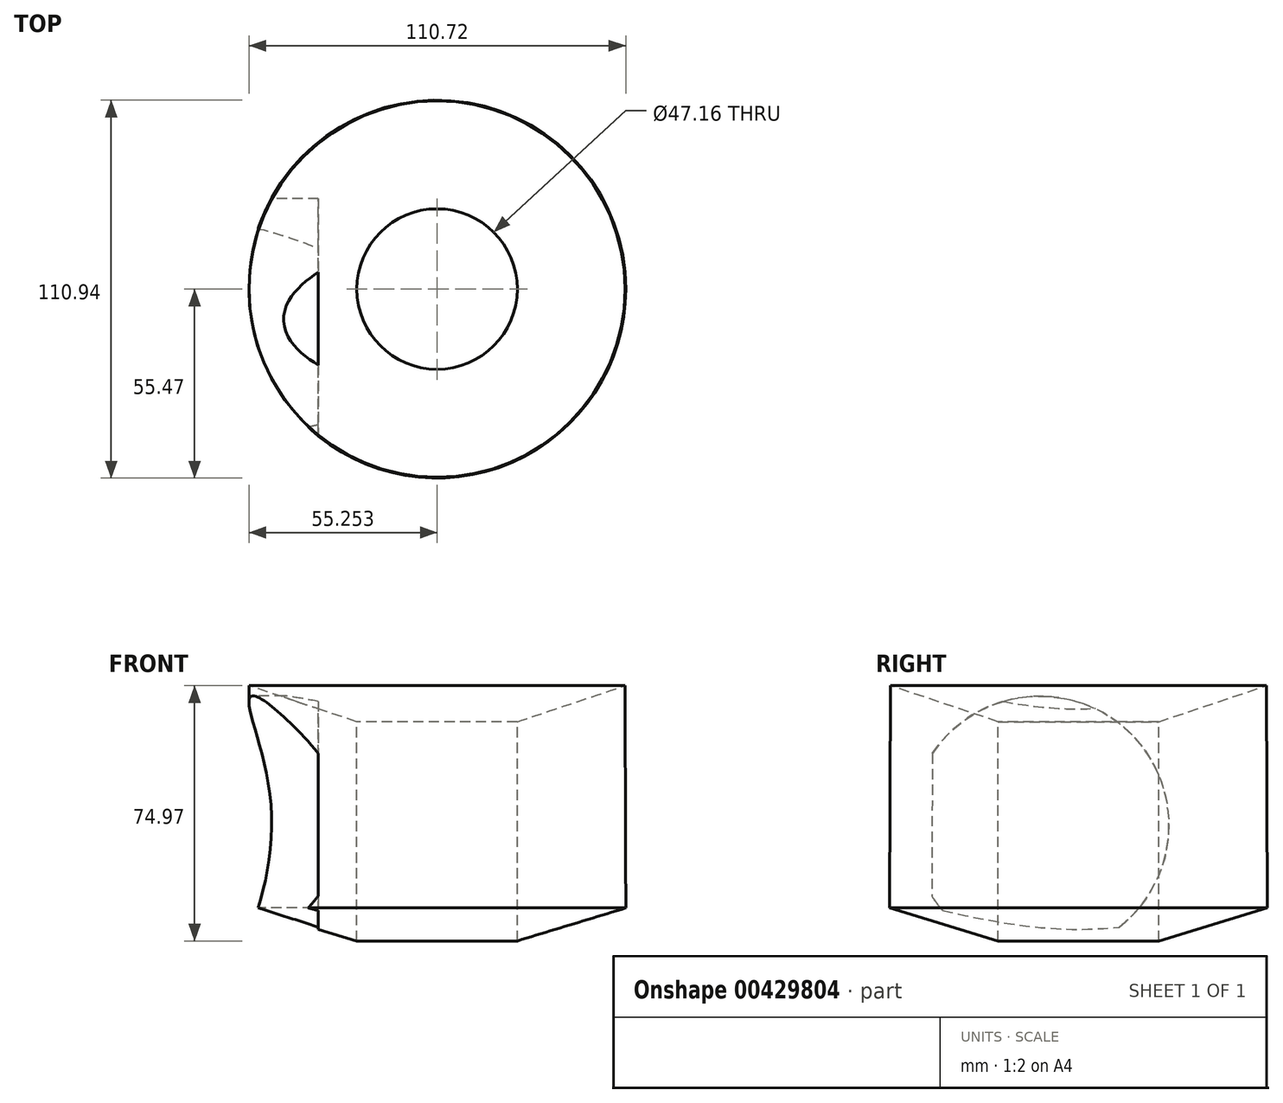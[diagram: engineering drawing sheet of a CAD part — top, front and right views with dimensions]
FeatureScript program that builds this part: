
annotation { "Feature Type Name" : "Feature", "Feature Type Description" : "" }
export const myFeature = defineFeature(function(context is Context, id is Id, definition is map)
    precondition{}
    {
        {
            var Q0;
            Q0=qCreatedBy(makeId("Front.planeOp"),FACE);
            var sketch = newSketch(context, id + "F0", { "sketchPlane" : qUnion([Q0])});
            skLineSegment(sketch, "E0", {"start": v(83.85, 105.73) * mm, "end": v(83.85, 41.36) * mm});
            skLineSegment(sketch, "E1", {"start": v(83.85, 41.36) * mm, "end": v(115.74, 51.05) * mm});
            skLineSegment(sketch, "E2", {"start": v(115.74, 51.05) * mm, "end": v(115.51, 116.33) * mm});
            skLineSegment(sketch, "E3", {"start": v(83.85, 105.73) * mm, "end": v(115.51, 116.33) * mm});
            skLineSegment(sketch, "E4", {"start": v(60.27, 122.71) * mm, "end": v(60.27, 52.44) * mm});
            skSolve(sketch);
        }
        {
            var Q0;
            Q0 = qSketchRegion(id + "F0", true);
            var Q1;
            Q1=sQuery(id+"F0.wireOp",EDGE,"E4");
            revolve(context, id + "F1", {"entities" : qUnion([Q0]), "axis" : qUnion([Q1]), "revolveType" : RevolveType.FULL});
        }
        {
            var Q0;
            Q0=qCreatedBy(makeId("Right.planeOp"),FACE);
            var sketch = newSketch(context, id + "F2", { "sketchPlane" : qUnion([Q0])});
            skCircle(sketch, "E5", {"center": v(-11.36, 75.35) * mm, "radius": 37.96 * mm});
            skSolve(sketch);
        }
        {
            var Q0;
            Q0 = qSketchRegion(id + "F2", true);
            extrude(context, id + "F3", {"entities" : qUnion([Q0]), "operationType" : NewBodyOperationType.REMOVE, "depth" : 25.4 * mm});
        }
    });
